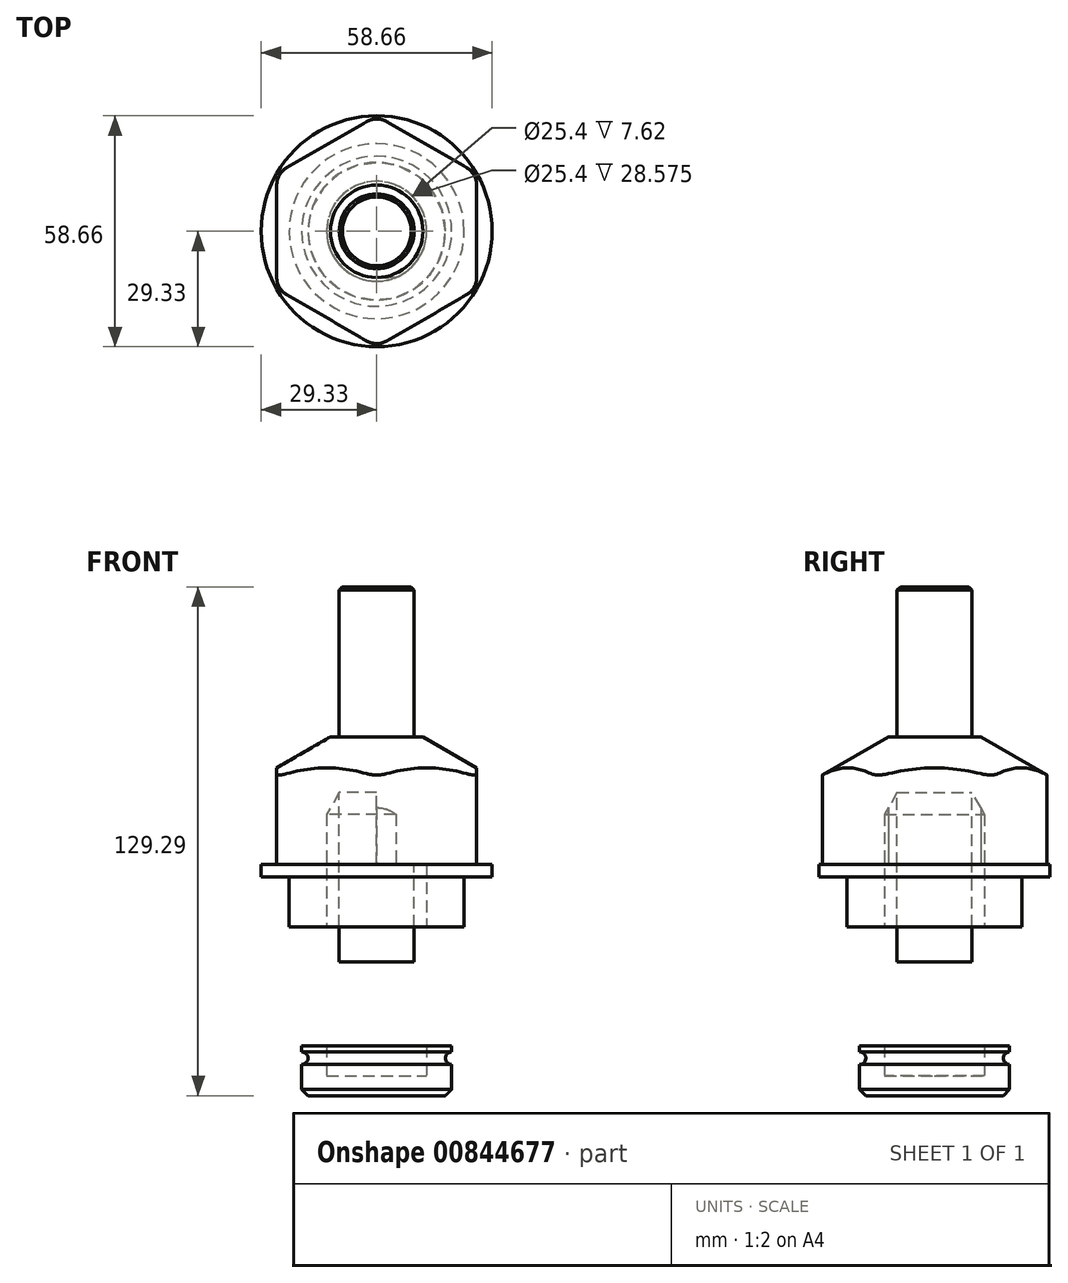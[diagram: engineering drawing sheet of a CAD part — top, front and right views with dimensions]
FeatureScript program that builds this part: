
annotation { "Feature Type Name" : "Feature", "Feature Type Description" : "" }
export const myFeature = defineFeature(function(context is Context, id is Id, definition is map)
    precondition{}
    {
        {
            var Q0;
            Q0=qCreatedBy(makeId("Top.planeOp"),FACE);
            var sketch = newSketch(context, id + "F0", { "sketchPlane" : qUnion([Q0])});
            skCircle(sketch, "E0", {"center": v(0, 0) * mm, "radius": 29.33 * mm});
            skLineSegment(sketch, "E1", {"start": v(0, 29.33) * mm, "end": v(0, -29.33) * mm, "construction": true});
            skLineSegment(sketch, "E2", {"start": v(-25.4, 14.66) * mm, "end": v(25.4, -14.66) * mm, "construction": true});
            skLineSegment(sketch, "E3", {"start": v(-25.4, -14.66) * mm, "end": v(25.4, 14.66) * mm, "construction": true});
            skLineSegment(sketch, "E4", {"start": v(-25.4, 14.66) * mm, "end": v(0, 29.33) * mm});
            skLineSegment(sketch, "E5", {"start": v(0, 29.33) * mm, "end": v(25.4, 14.66) * mm});
            skLineSegment(sketch, "E6", {"start": v(25.4, 14.66) * mm, "end": v(25.4, -14.66) * mm});
            skLineSegment(sketch, "E7", {"start": v(25.4, -14.66) * mm, "end": v(0, -29.33) * mm});
            skLineSegment(sketch, "E8", {"start": v(0, -29.33) * mm, "end": v(-25.4, -14.66) * mm});
            skLineSegment(sketch, "E9", {"start": v(-25.4, -14.66) * mm, "end": v(-25.4, 14.66) * mm});
            skCircle(sketch, "E10", {"center": v(0, 0) * mm, "radius": 7.94 * mm});
            skSolve(sketch);
        }
        {
            var Q0;
            Q0=makeQuery(id+"F0.imprint","IMPRINT",FACE,{"disambiguationData":[TD([[makeQuery(id+"F0.imprint","IMPRINT",EDGE,{"derivedFrom":sQuery(id+"F0.wireOp",EDGE,"E10")}),1.0]])]});
            var Q1;
            Q1=makeQuery(id+"F0.imprint","IMPRINT",FACE,{"disambiguationData":[TD([[makeQuery(id+"F0.imprint","IMPRINT",EDGE,{"derivedFrom":sQuery(id+"F0.wireOp",EDGE,"E4")}),-1.0]])]});
            extrude(context, id + "F1", {"entities" : qUnion([Q0, Q1]), "depth" : 35.56 * mm});
        }
        {
            var Q0;
            {var subQ0=sQuery(id+"F0.wireOp",EDGE,"E8");Q0=makeQuery(id+"F0.imprint","IMPRINT",FACE,{"disambiguationData":[TD([[makeQuery(id+"F0.imprint","IMPRINT",EDGE,{"derivedFrom":subQ0}),1.0]])]});}
            var Q1;
            {var subQ0=sQuery(id+"F0.wireOp",EDGE,"E7");Q1=makeQuery(id+"F0.imprint","IMPRINT",FACE,{"disambiguationData":[TD([[makeQuery(id+"F0.imprint","IMPRINT",EDGE,{"derivedFrom":subQ0}),1.0]])]});}
            var Q2;
            {var subQ0=sQuery(id+"F0.wireOp",EDGE,"E6");Q2=makeQuery(id+"F0.imprint","IMPRINT",FACE,{"disambiguationData":[TD([[makeQuery(id+"F0.imprint","IMPRINT",EDGE,{"derivedFrom":subQ0}),1.0]])]});}
            var Q3;
            Q3=makeQuery(id+"F0.imprint","IMPRINT",FACE,{"disambiguationData":[TD([[makeQuery(id+"F0.imprint","IMPRINT",EDGE,{"derivedFrom":sQuery(id+"F0.wireOp",EDGE,"E4")}),-1.0]])]});
            var Q4;
            {var subQ0=sQuery(id+"F0.wireOp",EDGE,"E5");Q4=makeQuery(id+"F0.imprint","IMPRINT",FACE,{"disambiguationData":[TD([[makeQuery(id+"F0.imprint","IMPRINT",EDGE,{"derivedFrom":subQ0}),1.0]])]});}
            var Q5;
            {var subQ0=sQuery(id+"F0.wireOp",EDGE,"E4");Q5=makeQuery(id+"F0.imprint","IMPRINT",FACE,{"disambiguationData":[TD([[makeQuery(id+"F0.imprint","IMPRINT",EDGE,{"derivedFrom":subQ0}),1.0]])]});}
            var Q6;
            {var subQ0=sQuery(id+"F0.wireOp",EDGE,"E9");Q6=makeQuery(id+"F0.imprint","IMPRINT",FACE,{"disambiguationData":[TD([[makeQuery(id+"F0.imprint","IMPRINT",EDGE,{"derivedFrom":subQ0}),1.0]])]});}
            extrude(context, id + "F2", {"entities" : qUnion([Q0, Q1, Q2, Q3, Q4, Q5, Q6]), "operationType" : NewBodyOperationType.ADD, "depth" : 3.17 * mm});
        }
        {
            var Q0;
            Q0=makeQuery(id+"F1.opExtrude","SWEPT_EDGE",EDGE,{"disambiguationData":[OSD([sQuery(id+"F0.wireOp",EDGE,"E0"),sQuery(id+"F0.wireOp",EDGE,"E7"),sQuery(id+"F0.wireOp",EDGE,"E8")])]});
            var Q1;
            Q1=makeQuery(id+"F1.opExtrude","SWEPT_EDGE",EDGE,{"disambiguationData":[OSD([sQuery(id+"F0.wireOp",EDGE,"E0"),sQuery(id+"F0.wireOp",EDGE,"E6"),sQuery(id+"F0.wireOp",EDGE,"E7")])]});
            var Q2;
            Q2=makeQuery(id+"F1.opExtrude","SWEPT_EDGE",EDGE,{"disambiguationData":[OSD([sQuery(id+"F0.wireOp",EDGE,"E0"),sQuery(id+"F0.wireOp",EDGE,"E5"),sQuery(id+"F0.wireOp",EDGE,"E6")])]});
            var Q3;
            Q3=makeQuery(id+"F1.opExtrude","SWEPT_EDGE",EDGE,{"disambiguationData":[OSD([sQuery(id+"F0.wireOp",EDGE,"E0"),sQuery(id+"F0.wireOp",EDGE,"E4"),sQuery(id+"F0.wireOp",EDGE,"E5")])]});
            var Q4;
            Q4=makeQuery(id+"F1.opExtrude","SWEPT_EDGE",EDGE,{"disambiguationData":[OSD([sQuery(id+"F0.wireOp",EDGE,"E0"),sQuery(id+"F0.wireOp",EDGE,"E4"),sQuery(id+"F0.wireOp",EDGE,"E9")])]});
            var Q5;
            Q5=makeQuery(id+"F1.opExtrude","SWEPT_EDGE",EDGE,{"disambiguationData":[OSD([sQuery(id+"F0.wireOp",EDGE,"E0"),sQuery(id+"F0.wireOp",EDGE,"E8"),sQuery(id+"F0.wireOp",EDGE,"E9")])]});
            fillet(context, id + "F3", {"entities" : qUnion([Q0, Q1, Q2, Q3, Q4, Q5]), "radius" : 5.08 * mm, "tangentPropagation" : true, "allowEdgeOverflow" : false});
        }
        {
            var Q0;
            Q0=qCreatedBy(makeId("Right.planeOp"),FACE);
            var sketch = newSketch(context, id + "F4", { "sketchPlane" : qUnion([Q0])});
            skLineSegment(sketch, "E11", {"start": v(0, 52) * mm, "end": v(0, 0) * mm, "construction": true});
            skLineSegment(sketch, "E12", {"start": v(11.73, 35.56) * mm, "end": v(35.4, 21.9) * mm});
            skLineSegment(sketch, "E13", {"start": v(35.4, 21.9) * mm, "end": v(35.4, 35.56) * mm});
            skLineSegment(sketch, "E14", {"start": v(35.4, 35.56) * mm, "end": v(11.73, 35.56) * mm});
            skLineSegment(sketch, "E15.0", {"start": v(11.73, 35.56) * mm, "end": v(-11.73, 35.56) * mm});
            skLineSegment(sketch, "E16.bottom", {"start": v(0, 0) * mm, "end": v(22.23, 0) * mm});
            skLineSegment(sketch, "E16.top", {"start": v(0, -12.7) * mm, "end": v(22.23, -12.7) * mm});
            skLineSegment(sketch, "E16.left", {"start": v(0, 0) * mm, "end": v(0, -12.7) * mm});
            skLineSegment(sketch, "E16.right", {"start": v(22.23, 0) * mm, "end": v(22.23, -12.7) * mm});
            skLineSegment(sketch, "E17.bottom", {"start": v(0, -12.7) * mm, "end": v(19.05, -12.7) * mm});
            skLineSegment(sketch, "E17.top", {"start": v(0, -27.69) * mm, "end": v(19.05, -27.69) * mm});
            skLineSegment(sketch, "E17.left", {"start": v(0, -12.7) * mm, "end": v(0, -27.69) * mm});
            skLineSegment(sketch, "E17.right", {"start": v(19.05, -12.7) * mm, "end": v(19.05, -27.69) * mm});
            skLineSegment(sketch, "E18.bottom", {"start": v(17.78, -27.69) * mm, "end": v(0, -27.69) * mm});
            skLineSegment(sketch, "E18.top", {"start": v(17.78, -42.93) * mm, "end": v(0, -42.93) * mm});
            skLineSegment(sketch, "E18.left", {"start": v(17.78, -27.69) * mm, "end": v(17.78, -42.93) * mm});
            skLineSegment(sketch, "E18.right", {"start": v(0, -27.69) * mm, "end": v(0, -42.93) * mm});
            skLineSegment(sketch, "E19.bottom", {"start": v(0, -42.93) * mm, "end": v(19.05, -42.93) * mm});
            skLineSegment(sketch, "E19.top", {"start": v(0, -55.63) * mm, "end": v(19.05, -55.63) * mm});
            skLineSegment(sketch, "E19.left", {"start": v(0, -42.93) * mm, "end": v(0, -55.63) * mm});
            skLineSegment(sketch, "E19.right", {"start": v(19.05, -42.93) * mm, "end": v(19.05, -55.63) * mm});
            skCircle(sketch, "E20", {"center": v(19.05, -24.51) * mm, "radius": 1.59 * mm});
            skCircle(sketch, "E21", {"center": v(19.05, -46.1) * mm, "radius": 1.59 * mm});
            skCircle(sketch, "E22", {"center": v(0, -17.46) * mm, "radius": 3.18 * mm});
            skCircle(sketch, "E23", {"center": v(0, -35.3) * mm, "radius": 3.18 * mm});
            skSolve(sketch);
        }
        {
            var Q0;
            Q0=makeQuery(id+"F4.imprint","IMPRINT",FACE,{"disambiguationData":[TD([[makeQuery(id+"F4.imprint","IMPRINT",EDGE,{"derivedFrom":sQuery(id+"F4.wireOp",EDGE,"E12")}),1.0]])]});
            var Q1;
            Q1=sQuery(id+"F4.wireOp",EDGE,"E11");
            revolve(context, id + "F5", {"operationType" : NewBodyOperationType.REMOVE, "entities" : qUnion([Q0]), "axis" : qUnion([Q1]), "revolveType" : RevolveType.FULL, "oppositeDirection" : true});
        }
        {
            var Q0;
            {var subQ7=sQuery(id+"F4.wireOp",EDGE,"E18.bottom");Q0=makeQuery(id+"F4.imprint","IMPRINT",FACE,{"disambiguationData":[TD([[makeQuery(id+"F4.imprint","IMPRINT",EDGE,{"derivedFrom":subQ7}),1.0]])]});}
            var Q1;
            {var subQ10=sQuery(id+"F4.wireOp",EDGE,"E17.bottom");Q1=makeQuery(id+"F4.imprint","IMPRINT",FACE,{"disambiguationData":[TD([[makeQuery(id+"F4.imprint","IMPRINT",EDGE,{"derivedFrom":subQ10}),-1.0]])]});}
            var Q2;
            Q2=makeQuery(id+"F4.imprint","IMPRINT",FACE,{"disambiguationData":[TD([[makeQuery(id+"F4.imprint","IMPRINT",EDGE,{"derivedFrom":sQuery(id+"F4.wireOp",EDGE,"E16.bottom")}),-1.0]])]});
            var Q3;
            {var subQ4=sQuery(id+"F4.wireOp",EDGE,"E19.top");Q3=makeQuery(id+"F4.imprint","IMPRINT",FACE,{"disambiguationData":[TD([[makeQuery(id+"F4.imprint","IMPRINT",EDGE,{"derivedFrom":subQ4}),1.0]])]});}
            var Q4;
            Q4=sQuery(id+"F4.wireOp",EDGE,"E11");
            revolve(context, id + "F6", {"operationType" : NewBodyOperationType.ADD, "entities" : qUnion([Q0, Q1, Q2, Q3]), "axis" : qUnion([Q4]), "revolveType" : RevolveType.FULL});
        }
        {
            var Q0;
            Q0=makeQuery(id+"F6.opRevolve","SWEPT_EDGE",EDGE,{"disambiguationData":[OSD([sQuery(id+"F4.wireOp",EDGE,"E19.top"),sQuery(id+"F4.wireOp",EDGE,"E19.right")])]});
            chamfer(context, id + "F7", {"entities" : qUnion([Q0]), "width" : 1.59 * mm, "tangentPropagation" : true});
        }
        {
            var Q0;
            {var subQ0=sQuery(id+"F4.wireOp",EDGE,"E16.right");var subQ1=sQuery(id+"F4.wireOp",EDGE,"E20");var subQ3=makeQuery(id+"F4.imprint","INTERSECT",VERTEX,{"disambiguationData":[OD(0.0)],"derivedFrom":[subQ0,subQ1]});Q0=makeQuery(id+"F4.imprint","IMPRINT",FACE,{"disambiguationData":[TD([[makeQuery(id+"F4.imprint","SKETCH_ENTITY",EDGE,{"disambiguationData":[TD([[subQ3,-1.0]])],"sketchEntityId":"E16.right"}),1.0]])]});}
            var Q1;
            {var subQ0=sQuery(id+"F4.wireOp",EDGE,"E20");var subQ1=sQuery(id+"F4.wireOp",EDGE,"E17.right");var subQ3=makeQuery(id+"F4.imprint","INTERSECT",VERTEX,{"disambiguationData":[OD(0.0)],"derivedFrom":[subQ1,subQ0]});Q1=makeQuery(id+"F4.imprint","IMPRINT",FACE,{"disambiguationData":[TD([[makeQuery(id+"F4.imprint","IMPRINT",EDGE,{"disambiguationData":[TD([[subQ3,-1.0]])],"derivedFrom":subQ1}),-1.0]])]});}
            var Q2;
            {var subQ0=sQuery(id+"F4.wireOp",EDGE,"E20");var subQ1=sQuery(id+"F4.wireOp",EDGE,"E17.right");var subQ3=makeQuery(id+"F4.imprint","INTERSECT",VERTEX,{"disambiguationData":[OD(0.0)],"derivedFrom":[subQ1,subQ0]});Q2=makeQuery(id+"F4.imprint","IMPRINT",FACE,{"disambiguationData":[TD([[makeQuery(id+"F4.imprint","IMPRINT",EDGE,{"disambiguationData":[TD([[subQ3,-1.0]])],"derivedFrom":subQ1}),1.0]])]});}
            var Q3;
            Q3=sQuery(id+"F4.wireOp",EDGE,"E11");
            revolve(context, id + "F8", {"entities" : qUnion([Q0, Q1, Q2]), "axis" : qUnion([Q3]), "revolveType" : RevolveType.FULL});
        }
        {
            var Q0;
            {var subQ0=sQuery(id+"F4.wireOp",EDGE,"E22");var subQ1=sQuery(id+"F4.wireOp",EDGE,"E17.left");var subQ3=makeQuery(id+"F4.imprint","INTERSECT",VERTEX,{"disambiguationData":[OD(0.0)],"derivedFrom":[subQ1,subQ0]});Q0=makeQuery(id+"F4.imprint","IMPRINT",FACE,{"disambiguationData":[TD([[makeQuery(id+"F4.imprint","IMPRINT",EDGE,{"disambiguationData":[TD([[subQ3,-1.0]])],"derivedFrom":subQ1}),-1.0]])]});}
            var Q1;
            {var subQ0=sQuery(id+"F4.wireOp",EDGE,"E22");var subQ1=sQuery(id+"F4.wireOp",EDGE,"E17.left");var subQ3=makeQuery(id+"F4.imprint","INTERSECT",VERTEX,{"disambiguationData":[OD(0.0)],"derivedFrom":[subQ1,subQ0]});Q1=makeQuery(id+"F4.imprint","IMPRINT",FACE,{"disambiguationData":[TD([[makeQuery(id+"F4.imprint","IMPRINT",EDGE,{"disambiguationData":[TD([[subQ3,-1.0]])],"derivedFrom":subQ1}),1.0]])]});}
            var Q2;
            {var subQ0=sQuery(id+"F4.wireOp",EDGE,"E23");var subQ1=sQuery(id+"F4.wireOp",EDGE,"E18.right");var subQ3=makeQuery(id+"F4.imprint","INTERSECT",VERTEX,{"disambiguationData":[OD(0.0)],"derivedFrom":[subQ1,subQ0]});Q2=makeQuery(id+"F4.imprint","IMPRINT",FACE,{"disambiguationData":[TD([[makeQuery(id+"F4.imprint","IMPRINT",EDGE,{"disambiguationData":[TD([[subQ3,-1.0]])],"derivedFrom":subQ1}),-1.0]])]});}
            var Q3;
            {var subQ0=sQuery(id+"F4.wireOp",EDGE,"E23");var subQ1=sQuery(id+"F4.wireOp",EDGE,"E18.right");var subQ3=makeQuery(id+"F4.imprint","INTERSECT",VERTEX,{"disambiguationData":[OD(0.0)],"derivedFrom":[subQ1,subQ0]});Q3=makeQuery(id+"F4.imprint","IMPRINT",FACE,{"disambiguationData":[TD([[makeQuery(id+"F4.imprint","IMPRINT",EDGE,{"disambiguationData":[TD([[subQ3,-1.0]])],"derivedFrom":subQ1}),1.0]])]});}
            extrude(context, id + "F9", {"entities" : qUnion([Q0, Q1, Q2, Q3]), "operationType" : NewBodyOperationType.REMOVE, "endBound" : BoundingType.THROUGH_ALL, "depth" : 25.4 * mm});
        }
        {
            var Q0;
            Q0=qCreatedBy(makeId("Right.planeOp"),FACE);
            var sketch = newSketch(context, id + "F10", { "sketchPlane" : qUnion([Q0])});
            skLineSegment(sketch, "E24", {"start": v(0, 73.66) * mm, "end": v(0, -50.55) * mm});
            skLineSegment(sketch, "E25", {"start": v(0, -50.55) * mm, "end": v(12.7, -50.55) * mm});
            skLineSegment(sketch, "E26", {"start": v(12.7, -50.55) * mm, "end": v(12.7, 15.88) * mm});
            skLineSegment(sketch, "E27", {"start": v(12.7, 15.88) * mm, "end": v(0, 15.88) * mm});
            skLineSegment(sketch, "E28", {"start": v(9.53, -21.6) * mm, "end": v(9.53, 73.66) * mm});
            skLineSegment(sketch, "E29", {"start": v(9.52, 73.66) * mm, "end": v(0, 73.66) * mm});
            skLineSegment(sketch, "E30", {"start": v(9.53, 21.37) * mm, "end": v(12.7, 15.88) * mm});
            skLineSegment(sketch, "E31.rect.bottom", {"start": v(12.7, -27.94) * mm, "end": v(-12.7, -27.94) * mm});
            skLineSegment(sketch, "E31.rect.top", {"start": v(12.7, -21.59) * mm, "end": v(-12.7, -21.59) * mm});
            skLineSegment(sketch, "E31.rect.left", {"start": v(12.7, -27.94) * mm, "end": v(12.7, -21.59) * mm});
            skLineSegment(sketch, "E31.rect.right", {"start": v(-12.7, -27.94) * mm, "end": v(-12.7, -21.59) * mm});
            skPoint(sketch, "E31.rect.middle", {"position": v(0, -24.77) * mm});
            skSolve(sketch);
        }
        {
            var Q0;
            {var subQ0=sQuery(id+"F10.wireOp",EDGE,"E29");Q0=makeQuery(id+"F10.imprint","IMPRINT",FACE,{"disambiguationData":[TD([[makeQuery(id+"F10.imprint","IMPRINT",EDGE,{"derivedFrom":subQ0}),1.0]])]});}
            var Q1;
            {var subQ0=sQuery(id+"F10.wireOp",EDGE,"E30");Q1=makeQuery(id+"F10.imprint","IMPRINT",FACE,{"disambiguationData":[TD([[makeQuery(id+"F10.imprint","IMPRINT",EDGE,{"derivedFrom":subQ0}),-1.0]])]});}
            var Q2;
            {var subQ1=sQuery(id+"F10.wireOp",EDGE,"E24");var subQ5=sQuery(id+"F10.wireOp",EDGE,"E27");var subQ7=makeQuery(id+"F10.imprint","INTERSECT",VERTEX,{"derivedFrom":[subQ1,subQ5]});Q2=makeQuery(id+"F10.imprint","IMPRINT",FACE,{"disambiguationData":[TD([[makeQuery(id+"F10.imprint","IMPRINT",EDGE,{"disambiguationData":[TD([[subQ7,-1.0]])],"derivedFrom":subQ1}),1.0]])]});}
            var Q3;
            {var subQ0=sQuery(id+"F10.wireOp",EDGE,"E31.rect.top");var subQ3=sQuery(id+"F10.wireOp",EDGE,"E28");var subQ4=makeQuery(id+"F10.imprint","INTERSECT",VERTEX,{"derivedFrom":[subQ3,subQ0]});Q3=makeQuery(id+"F10.imprint","IMPRINT",FACE,{"disambiguationData":[TD([[makeQuery(id+"F10.imprint","IMPRINT",EDGE,{"disambiguationData":[TD([[subQ4,-1.0]])],"derivedFrom":subQ3}),-1.0]])]});}
            var Q4;
            {var subQ5=sQuery(id+"F10.wireOp",EDGE,"E25");Q4=makeQuery(id+"F10.imprint","IMPRINT",FACE,{"disambiguationData":[TD([[makeQuery(id+"F10.imprint","IMPRINT",EDGE,{"derivedFrom":subQ5}),1.0]])]});}
            var Q5;
            {var subQ0=sQuery(id+"F10.wireOp",EDGE,"E31.rect.left");Q5=makeQuery(id+"F10.imprint","IMPRINT",FACE,{"disambiguationData":[TD([[makeQuery(id+"F10.imprint","IMPRINT",EDGE,{"derivedFrom":subQ0}),1.0]])]});}
            var Q6;
            Q6=sQuery(id+"F10.wireOp",EDGE,"E24");
            revolve(context, id + "F11", {"operationType" : NewBodyOperationType.REMOVE, "entities" : qUnion([Q0, Q1, Q2, Q3, Q4, Q5]), "axis" : qUnion([Q6]), "revolveType" : RevolveType.FULL, "oppositeDirection" : true});
        }
        {
            var Q0;
            {var subQ0=sQuery(id+"F10.wireOp",EDGE,"E29");Q0=makeQuery(id+"F10.imprint","IMPRINT",FACE,{"disambiguationData":[TD([[makeQuery(id+"F10.imprint","IMPRINT",EDGE,{"derivedFrom":subQ0}),1.0]])]});}
            var Q1;
            {var subQ1=sQuery(id+"F10.wireOp",EDGE,"E24");var subQ5=sQuery(id+"F10.wireOp",EDGE,"E27");var subQ7=makeQuery(id+"F10.imprint","INTERSECT",VERTEX,{"derivedFrom":[subQ1,subQ5]});Q1=makeQuery(id+"F10.imprint","IMPRINT",FACE,{"disambiguationData":[TD([[makeQuery(id+"F10.imprint","IMPRINT",EDGE,{"disambiguationData":[TD([[subQ7,-1.0]])],"derivedFrom":subQ1}),1.0]])]});}
            var Q2;
            {var subQ0=sQuery(id+"F10.wireOp",EDGE,"E31.rect.left");Q2=makeQuery(id+"F10.imprint","IMPRINT",FACE,{"disambiguationData":[TD([[makeQuery(id+"F10.imprint","IMPRINT",EDGE,{"derivedFrom":subQ0}),1.0]])]});}
            var Q3;
            Q3=sQuery(id+"F10.wireOp",EDGE,"E24");
            revolve(context, id + "F12", {"entities" : qUnion([Q0, Q1, Q2]), "axis" : qUnion([Q3]), "revolveType" : RevolveType.FULL});
        }
        {
            var Q0;
            Q0=makeQuery(id+"F12.opRevolve","SWEPT_EDGE",EDGE,{"disambiguationData":[OSD([sQuery(id+"F10.wireOp",EDGE,"E28"),sQuery(id+"F10.wireOp",EDGE,"E29")])]});
            chamfer(context, id + "F13", {"entities" : qUnion([Q0]), "width" : 0.8 * mm, "tangentPropagation" : true});
        }
        {
            var Q0;
            Q0=makeQuery(id+"F1.opExtrude","SWEPT_FACE",FACE,{"disambiguationData":[OSD([sQuery(id+"F0.wireOp",EDGE,"E6")])]});
            extrude(context, id + "F14", {"entities" : qUnion([Q0]), "operationType" : NewBodyOperationType.ADD, "oppositeDirection" : true, "depth" : 25.4 * mm, "offsetDistance" : 25.4 * mm});
        }
    });
